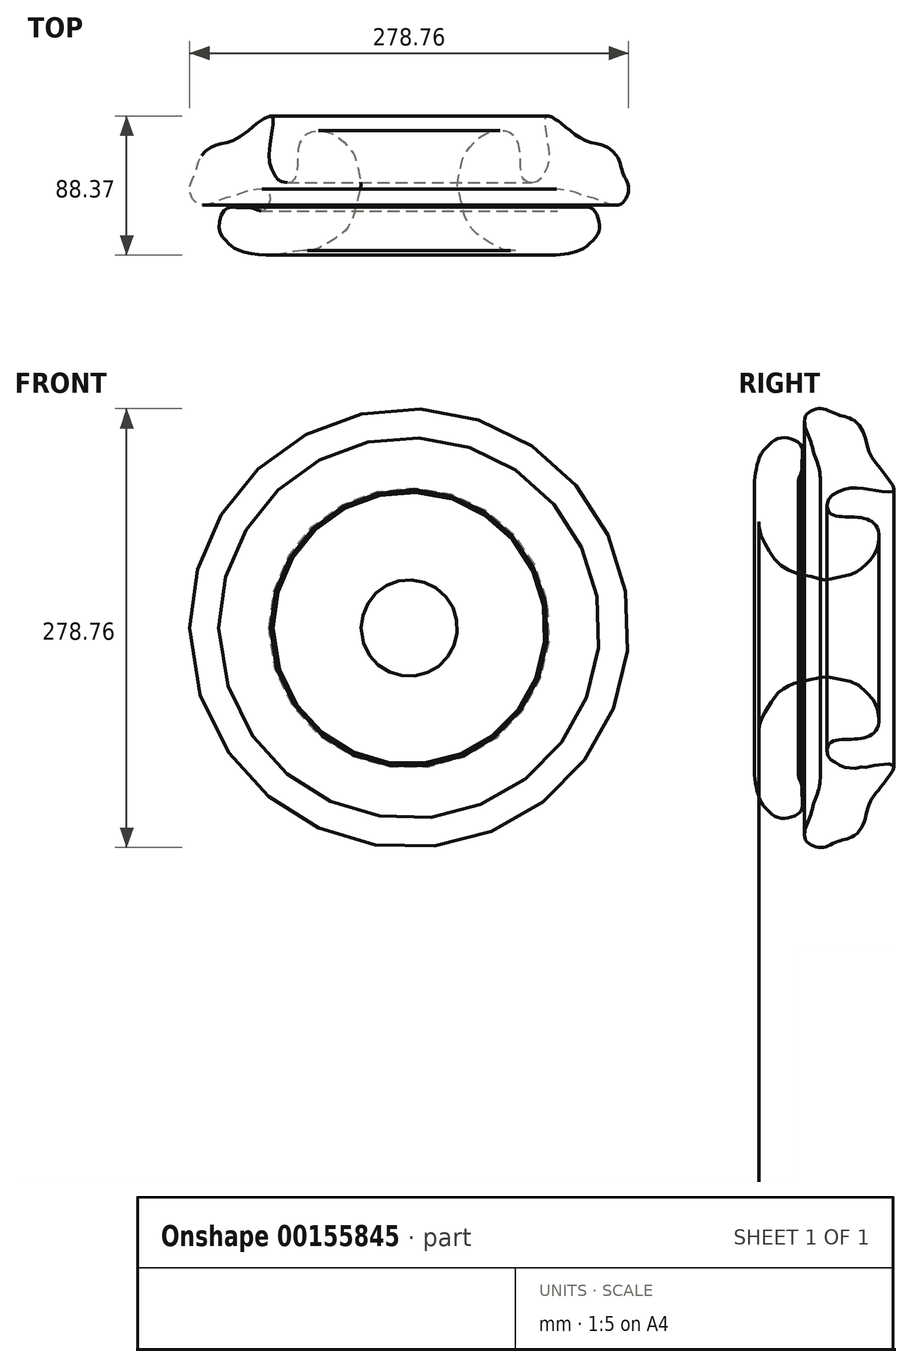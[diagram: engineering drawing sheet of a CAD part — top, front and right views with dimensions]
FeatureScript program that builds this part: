
annotation { "Feature Type Name" : "Feature", "Feature Type Description" : "" }
export const myFeature = defineFeature(function(context is Context, id is Id, definition is map)
    precondition{}
    {
        {
            var Q0;
            Q0=qCreatedBy(makeId("Top.planeOp"),FACE);
            var sketch = newSketch(context, id + "F0", { "sketchPlane" : qUnion([Q0])});
            skFitSpline(sketch, "E0", {"points": [v(-51.57, 37.07) * mm, v(-41.6, 43.8) * mm, v(-28.48, 48.21) * mm, v(-7.2, 61.85) * mm, v(-8.9, 36.53) * mm, v(-5.28, 24.97) * mm, v(-2.02, 20.94) * mm, v(7, 21.3) * mm, v(9.93, 40.18) * mm, v(16.64, 51.57) * mm, v(34.09, 49.32) * mm, v(44.5, 38.67) * mm, v(45.63, 36.81) * mm, v(49.52, 18.87) * mm, v(49.47, 17.3) * mm, v(46.25, 4.11) * mm, v(45.37, 0) * mm, v(41.44, -8.3) * mm, v(34.03, -15.14) * mm, v(18.8, -23.15) * mm, v(11.55, -23.47) * mm, v(-9.9, -26.3) * mm, v(-30.1, -22.3) * mm, v(-34.81, -18.5) * mm, v(-40.54, -10.15) * mm, v(-36.21, 3.04) * mm, v(-28.25, 3.82) * mm, v(-18.92, 3.4) * mm, v(-13.29, 1.75) * mm, v(-7.93, 8.48) * mm, v(-9.86, 14.73) * mm, v(-16.82, 15.27) * mm, v(-24.5, 13.73) * mm, v(-31.3, 11.16) * mm, v(-37.4, 9.65) * mm, v(-53.5, 5.76) * mm, v(-59.17, 16.45) * mm, v(-55.89, 25.08) * mm, v(-51.57, 37.07) * mm]});
            skLineSegment(sketch, "E1", {"start": v(80.2, 42.26) * mm, "end": v(80.2, -6.34) * mm});
            skSolve(sketch);
        }
        {
            var Q0;
            Q0=makeQuery(id+"F0.imprint","IMPRINT",FACE,{"disambiguationData":[TD([[makeQuery(id+"F0.imprint","IMPRINT",EDGE,{"derivedFrom":sQuery(id+"F0.wireOp",EDGE,"E0")}),-1.0]])]});
            var Q1;
            Q1=sQuery(id+"F0.wireOp",EDGE,"E1");
            revolve(context, id + "F1", {"entities" : qUnion([Q0]), "axis" : qUnion([Q1]), "revolveType" : RevolveType.FULL});
        }
    });
